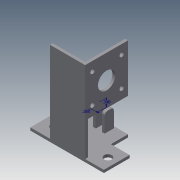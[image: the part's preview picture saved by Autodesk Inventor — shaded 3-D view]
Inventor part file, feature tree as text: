
AUTODESK INVENTOR PART (.ipt)
format: ipt  version: 2016 (Build 200138000, 138)  size: 162,304 bytes
history: native  units: in
note: dims shown in document units (in); Inventor stores cm internally (conversion verified against a paired STEP export)
features: extrude x5, sketch x5, plane x1, fillet x1, draft x1
ambient origin geometry x8: Origin, YZ Plane, XZ Plane, XY Plane, X Axis, Y Axis, Z Axis, Center Point
bodies: Solid1 (feature_tree)
feature tree (13):
  extrude  "Extrusion1"  Depth=3.1496in
  plane  "Work Plane1"
  extrude  "Extrusion3"  Depth=0.3268in
  extrude  "Extrusion5"  Depth=0.1181in
  fillet  "Fillet1"  Radius=0.1181in
  extrude  "Extrusion6"  Depth=0.1181in TaperAngle=0.0deg
  draft  "FaceDraft1"
  extrude  "Extrusion7"  Depth=0.1181in
  sketch  "Sketch1"  dims[d0=1.1024in d1=3.1496in]
  sketch  "Sketch3"  dims[d2=0.3268in d3=0.3268in]
  sketch  "Sketch5"  dims[d4=0.5512in d5=0.5512in d6=0.1181in d7=0.0in]
  sketch  "Sketch6"  dims[d10=0.7874in d12=1.2205in d13=0.7874in d15=1.2205in d18=0.1181in d19=0.0in]
  sketch  "Sketch8"  dims[d22=0.1181in d23=0.1181in d24=0.26in d25=0.7087in d26=0.0in d27=0.3937in d28=0.125in d29=0.1875in d30=0.2in d31=0.3937in d32=0.0in d33=0.2405in d34=0.8858in d35=0.6102in d36=0.6102in d37=0.3937in d38=0.0in]
